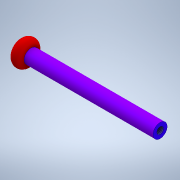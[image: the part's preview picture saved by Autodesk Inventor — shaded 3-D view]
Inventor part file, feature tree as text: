
AUTODESK INVENTOR PART (.ipt)
format: ipt  version: 2021 (Build 250183000, 183)  size: 130,048 bytes
history: native  units: mm
features: revolve x1, thread x1, sketch x1
ambient origin geometry x8: Origin, YZ Plane, XZ Plane, XY Plane, X Axis, Y Axis, Z Axis, Center Point
bodies: Solid1 (feature_tree)
feature tree (3):
  revolve  "Revolution1"  [1 undecoded]
  thread  "Thread1"  [1 undecoded]
  sketch  "Sketch1"  dims[d0=100.0mm d1=5.0mm d2=92.0mm d3=4.0mm d4=12.0mm d5=120.0deg d6=2.38mm d7=90.0deg d8=12.0mm d9=0.0mm]
note: 2 required parameter values undecoded (feature->parameter linkage not recoverable at this tier; creation-order binding heuristic only, values carry confidence <= 0.55)